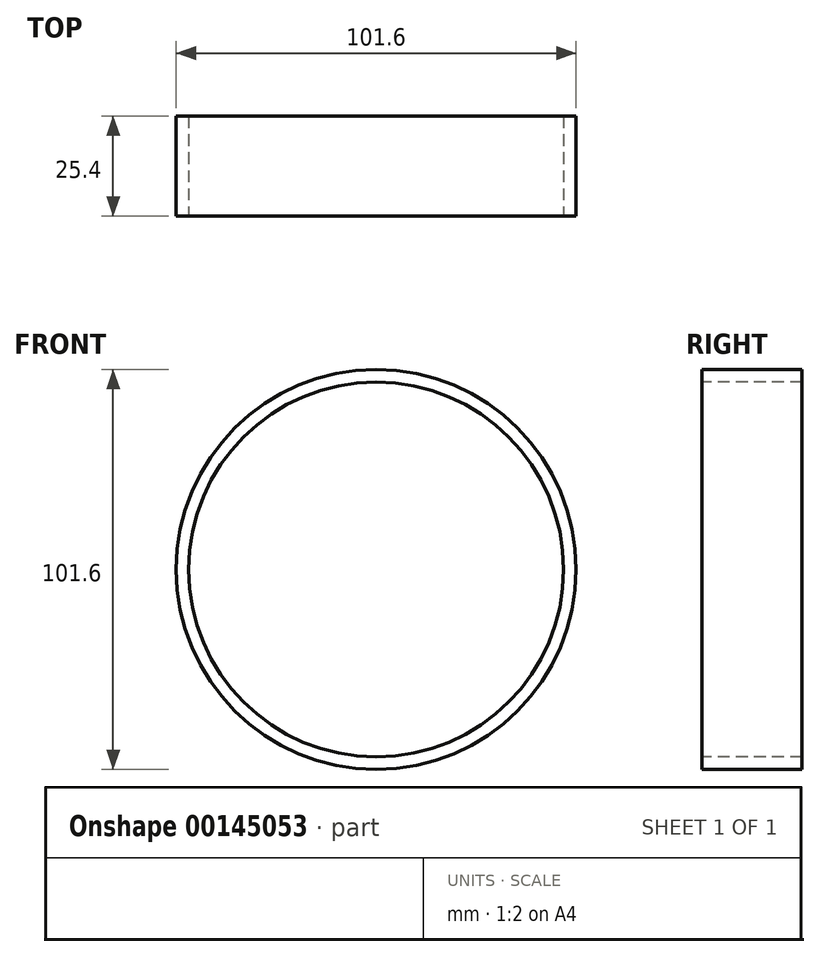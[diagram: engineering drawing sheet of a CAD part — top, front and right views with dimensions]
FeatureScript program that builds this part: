
annotation { "Feature Type Name" : "Feature", "Feature Type Description" : "" }
export const myFeature = defineFeature(function(context is Context, id is Id, definition is map)
    precondition{}
    {
        {
            var Q0;
            Q0=qCreatedBy(makeId("Front.planeOp"),FACE);
            var sketch = newSketch(context, id + "F0", { "sketchPlane" : qUnion([Q0])});
            skCircle(sketch, "E0", {"center": v(0, 0) * mm, "radius": 50.8 * mm});
            skCircle(sketch, "E1", {"center": v(0, 0) * mm, "radius": 47.63 * mm});
            skCircle(sketch, "E2", {"center": v(0, 0) * mm, "radius": 36.51 * mm});
            skSolve(sketch);
        }
        {
            var Q0;
            Q0=sQuery(id+"F0.wireOp",EDGE,"E1");
            var Q1;
            Q1=sQuery(id+"F0.wireOp",EDGE,"E0");
            extrude(context, id + "F1", {"bodyType" : ToolBodyType.SURFACE, "surfaceEntities" : qUnion([Q0, Q1]), "depth" : 25.4 * mm});
        }
    });
